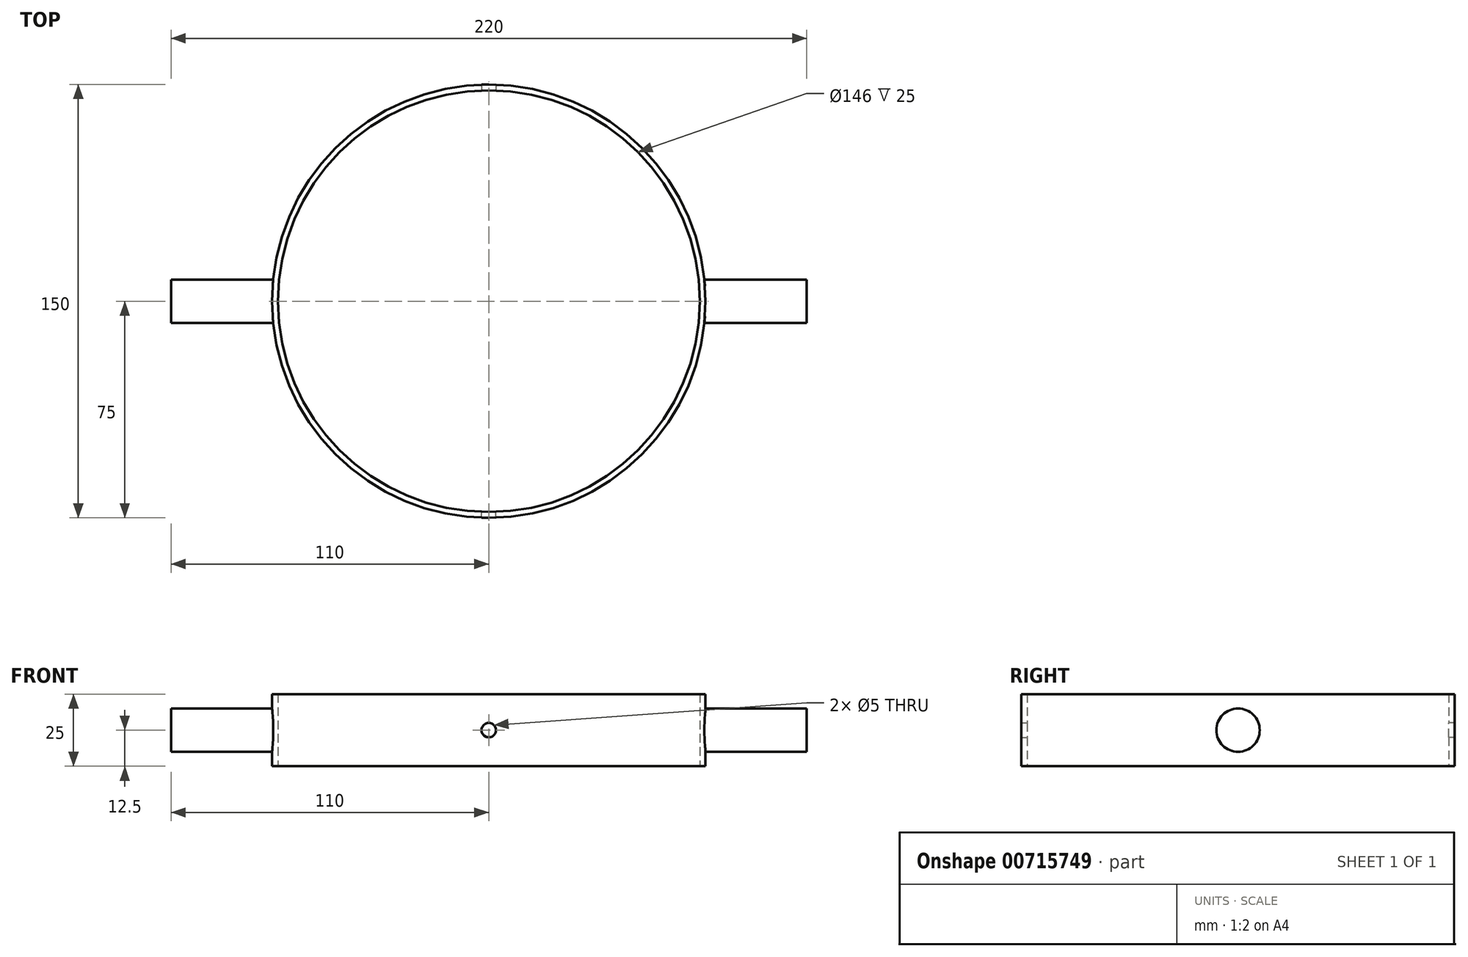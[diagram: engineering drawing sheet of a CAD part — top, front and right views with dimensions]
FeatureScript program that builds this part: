
annotation { "Feature Type Name" : "Feature", "Feature Type Description" : "" }
export const myFeature = defineFeature(function(context is Context, id is Id, definition is map)
    precondition{}
    {
        {
            var Q0;
            Q0=qCreatedBy(makeId("Top.planeOp"),FACE);
            var sketch = newSketch(context, id + "F0", { "sketchPlane" : qUnion([Q0])});
            skCircle(sketch, "E0", {"center": v(0, 0) * mm, "radius": 75 * mm});
            skCircle(sketch, "E1", {"center": v(0, 0) * mm, "radius": 73 * mm});
            skSolve(sketch);
        }
        {
            var Q0;
            Q0 = qSketchRegion(id + "F0", true);
            extrude(context, id + "F1", {"entities" : qUnion([Q0]), "depth" : 25 * mm, "offsetDistance" : 25 * mm, "symmetric" : true});
        }
        {
            var Q0;
            Q0=qCreatedBy(makeId("Front.planeOp"),FACE);
            var sketch = newSketch(context, id + "F2", { "sketchPlane" : qUnion([Q0])});
            skCircle(sketch, "E2", {"center": v(0, 0) * mm, "radius": 2.5 * mm});
            skSolve(sketch);
        }
        {
            var Q0;
            Q0 = qSketchRegion(id + "F2", true);
            extrude(context, id + "F3", {"entities" : qUnion([Q0]), "operationType" : NewBodyOperationType.REMOVE, "endBound" : BoundingType.THROUGH_ALL, "oppositeDirection" : true, "depth" : 25 * mm, "offsetDistance" : 25 * mm});
        }
        {
            var Q0;
            Q0 = qSketchRegion(id + "F2", true);
            extrude(context, id + "F4", {"entities" : qUnion([Q0]), "operationType" : NewBodyOperationType.REMOVE, "endBound" : BoundingType.THROUGH_ALL, "depth" : 25 * mm, "offsetDistance" : 25 * mm});
        }
        {
            var Q0;
            Q0=qCreatedBy(makeId("Right.planeOp"),FACE);
            var sketch = newSketch(context, id + "F5", { "sketchPlane" : qUnion([Q0])});
            skCircle(sketch, "E3", {"center": v(0, 0) * mm, "radius": 7.5 * mm});
            skSolve(sketch);
        }
        {
            var Q0;
            Q0 = qSketchRegion(id + "F5", true);
            var Q1;
            Q1=makeQuery(id+"F1.opExtrude","SWEPT_FACE",FACE,{"disambiguationData":[OSD([sQuery(id+"F0.wireOp",EDGE,"E0")])]});
            var Q2;
            Q2=makeQuery(id+"F1.opExtrude","SWEPT_BODY",BODY,{"disambiguationData":[OSD([sQuery(id+"F0.wireOp",EDGE,"E0"),sQuery(id+"F0.wireOp",EDGE,"E1")])]});
            var Q3;
            Q3=makeQuery(id+"F1.opExtrude","SWEPT_FACE",FACE,{"disambiguationData":[OSD([sQuery(id+"F0.wireOp",EDGE,"E0")])]});
            extrude(context, id + "F6", {"entities" : qUnion([Q0]), "depth" : 110 * mm, "endBoundEntityFace" : qUnion([Q1]), "endBoundEntityBody" : qUnion([Q2]), "offsetDistance" : -250 * mm});
        }
        {
            var Q0;
            Q0 = qSketchRegion(id + "F5", true);
            var Q1;
            Q1=makeQuery(id+"F1.opExtrude","SWEPT_FACE",FACE,{"disambiguationData":[OSD([sQuery(id+"F0.wireOp",EDGE,"E1")])]});
            extrude(context, id + "F7", {"entities" : qUnion([Q0]), "operationType" : NewBodyOperationType.REMOVE, "endBound" : BoundingType.UP_TO_SURFACE, "depth" : 25 * mm, "endBoundEntityFace" : qUnion([Q1]), "offsetDistance" : 25 * mm});
        }
        {
            var Q0;
            Q0=makeQuery(id+"F6.opExtrude","SWEPT_BODY",BODY,{"disambiguationData":[OSD([sQuery(id+"F5.wireOp",EDGE,"E3")])]});
            var Q1;
            Q1=qCreatedBy(makeId("Right.planeOp"),FACE);
            mirror(context, id + "F8", {"operationType" : NewBodyOperationType.ADD, "entities" : qUnion([Q0]), "mirrorPlane" : qUnion([Q1])});
        }
    });
